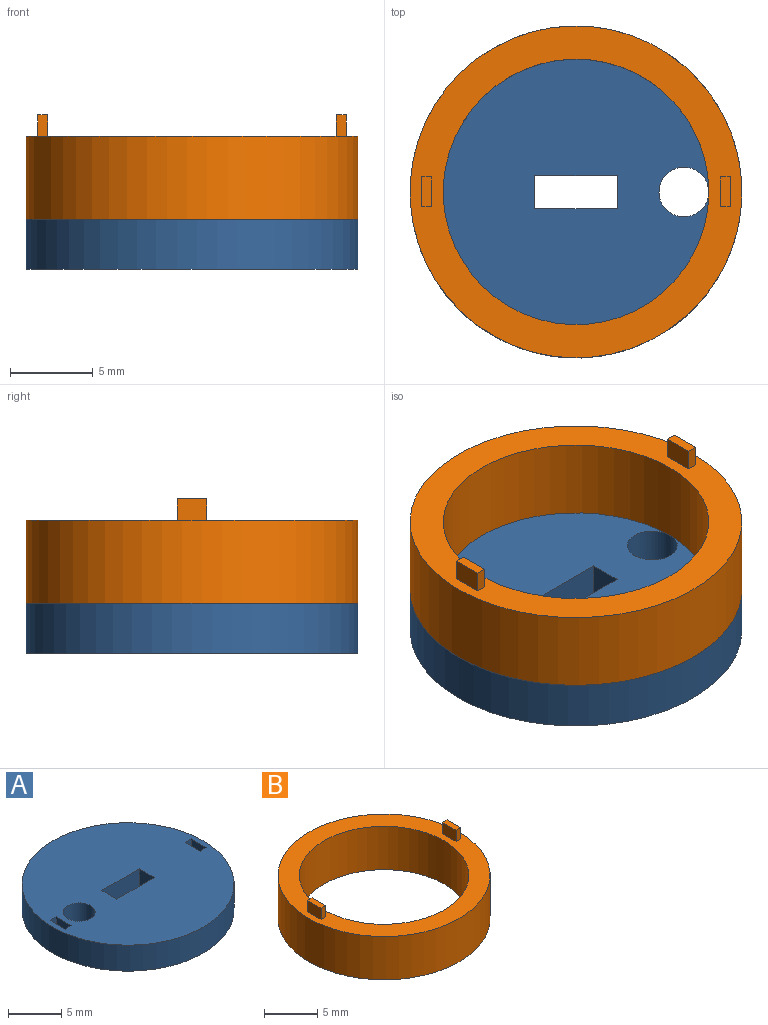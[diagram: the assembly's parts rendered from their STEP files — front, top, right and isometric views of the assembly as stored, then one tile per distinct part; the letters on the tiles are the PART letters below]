
ASSEMBLY  parts=2 mates=1
PART A: 18 faces, bbox 20x20x3 mm
  f0: plane 5x3mm, normal (0,1,0), area 15mm2, adj f1,f9,f14,f15
  f1: plane 3x2mm, normal (1,0,0), area 6mm2, adj f0,f2,f14,f15
  f2: plane 5x3mm, normal (0,-1,0), area 15mm2, adj f1,f9,f14,f15
  f3: plane 2x1.5mm, normal (1,0,0), area 3mm2, adj f4,f10,f14,f17
  f4: plane 1.5x0.8mm, normal (0,-1,0), area 1.2mm2, adj f3,f5,f14,f17
  f5: plane 2x1.5mm, normal (-1,0,0), area 3mm2, adj f4,f10,f14,f17
  f6: plane 2x1.5mm, normal (1,0,0), area 3mm2, adj f7,f11,f14,f16
  f7: plane 1.5x0.8mm, normal (0,-1,0), area 1.2mm2, adj f6,f8,f14,f16
  f8: plane 2x1.5mm, normal (-1,0,0), area 3mm2, adj f7,f11,f14,f16
  f9: plane 3x2mm, normal (-1,0,0), area 6mm2, adj f0,f2,f14,f15
  f10: plane 1.5x0.8mm, normal (0,1,0), area 1.2mm2, adj f3,f5,f14,f17
  f11: plane 1.5x0.8mm, normal (0,1,0), area 1.2mm2, adj f6,f8,f14,f16
  f12: cylinder r=1.5mm len=3mm, axis (0,0,-1), area 28.3mm2, adj f14,f15
  f13: cylinder r=10mm len=20mm, axis (0,0,-1), area 188.5mm2, adj f14,f15
  f14: plane 20x20mm, normal (0,0,1), area 293.9mm2, adj f0,f1,f2,f3,f4,f5,f6,f7
  f15: plane 20x20mm, normal (0,0,-1), area 297.1mm2, adj f0,f1,f2,f9,f12,f13
  f16: plane 2x0.8mm, normal (0,0,1), area 1.6mm2, adj f6,f7,f8,f11
  f17: plane 2x0.8mm, normal (0,0,1), area 1.6mm2, adj f3,f4,f5,f10
PART B: 14 faces, bbox 20x20x6.3 mm
  f0: plane 1.8x1.3mm, normal (-1,0,0), area 2.3mm2, adj f1,f3,f4,f12
  f1: plane 1.3x0.6mm, normal (0,-1,0), area 0.8mm2, adj f0,f2,f4,f12
  f2: plane 1.8x1.3mm, normal (1,0,0), area 2.3mm2, adj f1,f3,f4,f12
  f3: plane 1.3x0.6mm, normal (0,1,0), area 0.8mm2, adj f0,f2,f4,f12
  f4: plane 1.8x0.6mm, normal (0,0,1), area 1.1mm2, adj f0,f1,f2,f3
  f5: plane 1.8x1.3mm, normal (-1,0,0), area 2.3mm2, adj f6,f8,f9,f12
  f6: plane 1.3x0.6mm, normal (0,-1,0), area 0.8mm2, adj f5,f7,f9,f12
  f7: plane 1.8x1.3mm, normal (1,0,0), area 2.3mm2, adj f6,f8,f9,f12
  f8: plane 1.3x0.6mm, normal (0,1,0), area 0.8mm2, adj f5,f7,f9,f12
  f9: plane 1.8x0.6mm, normal (0,0,1), area 1.1mm2, adj f5,f6,f7,f8
  f10: cylinder r=8mm len=16mm, axis (0,0,-1), area 251.3mm2, adj f12,f13
  f11: cylinder r=10mm len=20mm, axis (0,0,-1), area 314.2mm2, adj f12,f13
  f12: plane 20x20mm, normal (0,0,1), area 110.9mm2, adj f0,f1,f2,f3,f5,f6,f7,f8
  f13: plane 20x20mm, normal (0,0,-1), area 113.1mm2, adj f10,f11
PLACE A rot(axis=(0,1,0),180deg) t=(-12.74,2.2,4.36)mm
PLACE B t=(-12.74,2.2,4.36)mm
MATE fastened A.f13 <-> B.f10  axis (0,0,1) through (-12.74,2.2,4.36)mm
